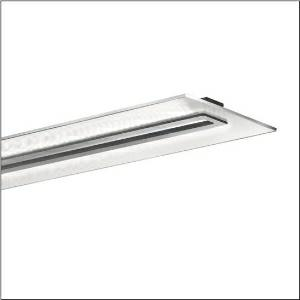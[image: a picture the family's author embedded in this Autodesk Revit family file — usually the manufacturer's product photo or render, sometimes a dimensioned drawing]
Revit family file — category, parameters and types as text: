
# Revit family: vega_r__11_5mn238dlc0s_c747
name_source: partatom
category: Lighting Fixtures
units: mm (PartAtom-declared; Revit-internal decimal feet)

## family parameters
Cut with Voids When Loaded = No
Host = Face
Light Source = No
Part Type = Normal
Room Calculation Point = No
Round Connector Dimension = Use Diameter
Shared = No

## types (1)
- --- (1 x LED 4000K / CRI = 80 (unbekannt), 4300 lm, 4000K)
    Apparent Load = 31 VA
    CIE Flux Codes = 61 86 97 62 100
    Color Rendering = 80
    Color Temperature = 4000K
    Default Elevation = 1800 mm
    Description = Vega® 11, office luminaire, primary light control with prismatic reflector, of PMMA, transparent prismatic structure, CAT 2 (L<= 1500cd/m²), light emission: direct/indirect distribution, primary light characteristic: symmetric, installation type: suspended mounting, surface-mounted, LED, rated luminous flux: 4.300lm, luminous efficacy: 139lm/W, light colour: 840, colour temperature: 4000K, control gear: DALI, with terminal, 3+2-pole, max. 2.5mm², mains connection: 230V, AC, 50Hz, connection cable inclusive, cable length: 1,5m, rated input power: 31W, luminaire housing, rectangular, rounded, of aluminium section, anodised, metallic grey (RAL 9006), length: 1.250mm, width: 350mm, height: 43mm, luminaire housing, lower part, of aluminium section, anodised, metallic grey (RAL 9006), of PC, grey, protection rating (complete): IP20, insulation class (complete): insulation class I (protective earthing), certification: CE, permissible operating ambient temperature: 0..+35°C, standard: EN 50419, packaging unit: 1 piece
    Height = 40 mm  [stored 0.131234 ft]
    Lamp = 1 x LED 4000K / CRI >= 80 (unbekannt)
    Lamp Light Flux = 4300 lm
    Lamp count = 1
    Length = 1250 mm
    Luminous efficacy = 139 lm/W
    Manufacturer = Siteco
    ModVariant = No
    Model = 5MN238DLC0S
    Mounting Place = Ceiling
    Mounting Type = Pendant
    Number of Poles = 1
    OnlyDefault = Yes
    Power Factor = 1
    Product Name = Vega® 11
    Product group = office luminaire | ceiling pendant
    ProductGroupID = 903
    Protection Class = Protection class I
    Protection Degree = IP 20
    RLX_Detail_Level = 1
    RLX_Emergency_Light_Flux = 0 lm
    RLX_Emergency_Type = 0
    RLX_Emergency_Type_DB = No
    RlxData = <blob elided: 62873 chars, md5=829696af>
    Socket = socket
    Standby Power = 0 W
    System Light Flux = 4300 lm
    System Power = 31 W
    Type Comments = factory setting: luminous flux: 100 % | dim-lin: 254 | 231 mA
    Type Image = l_1004807.jpg
    URL = http://relux.com
    VarID = @adj_220961
    Voltage = 0 V
    Weight = 0.00 kg
    Width = 350 mm

note: [stored X ft] marks values corroborated as IEEE doubles in the binary element streams (Revit-internal decimal feet)

## geometry (parser evidence)
native form markers: Blend x4, Sweep x13
no freeform markers — native parametric forms only
